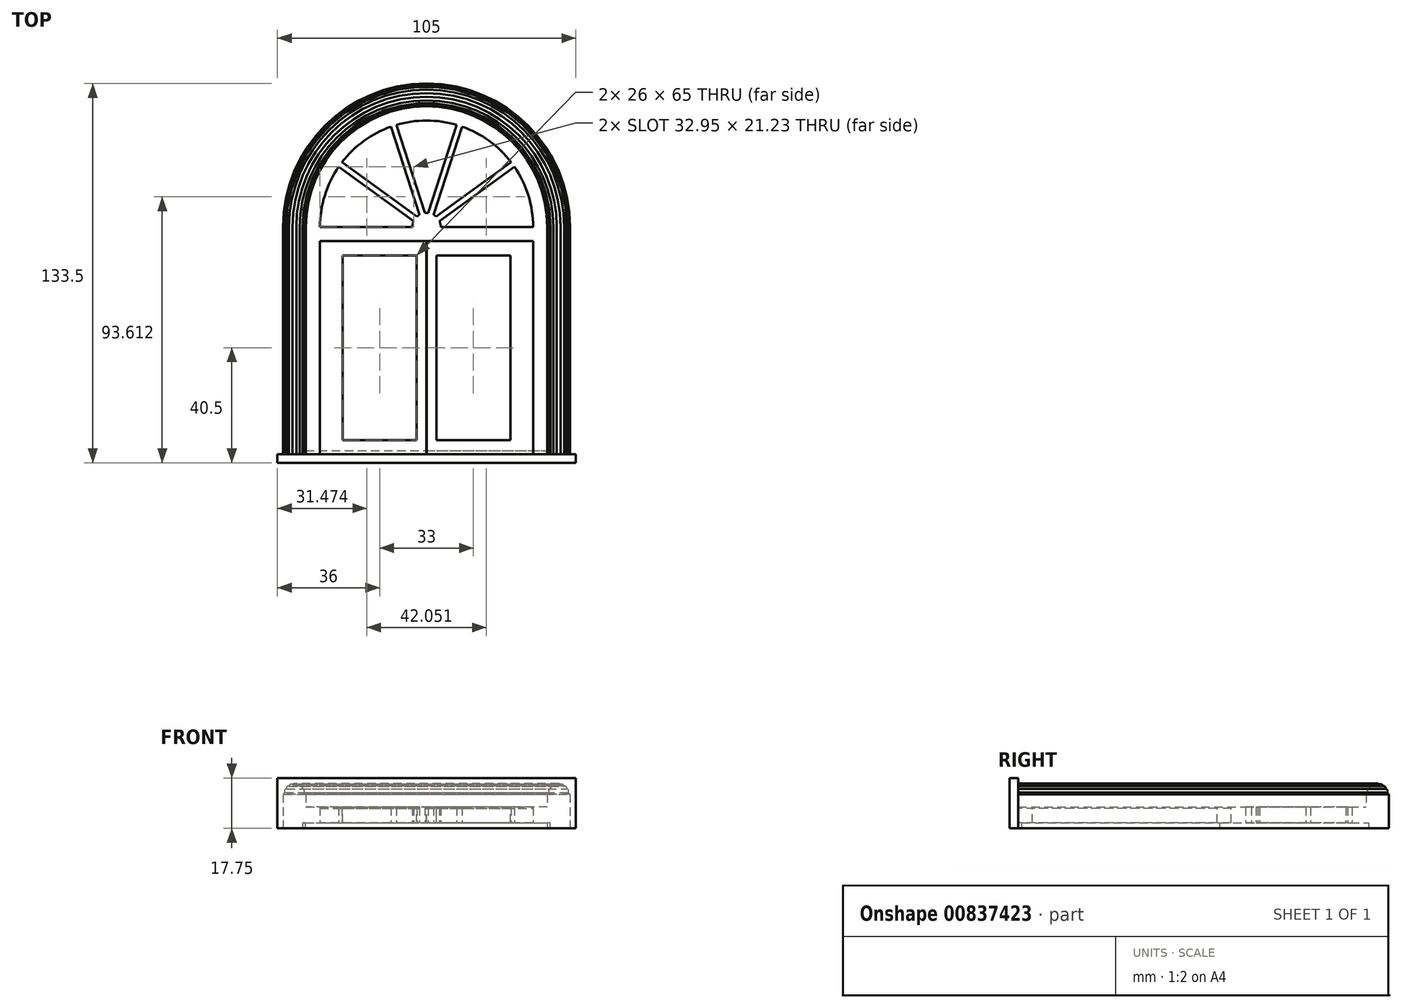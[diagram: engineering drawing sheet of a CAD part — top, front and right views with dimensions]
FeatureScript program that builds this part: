
annotation { "Feature Type Name" : "Feature", "Feature Type Description" : "" }
export const myFeature = defineFeature(function(context is Context, id is Id, definition is map)
    precondition{}
    {
        {
            var Q0;
            Q0=qCreatedBy(makeId("Top.planeOp"),FACE);
            var sketch = newSketch(context, id + "F0", { "sketchPlane" : qUnion([Q0])});
            skLineSegment(sketch, "E0.bottom", {"start": v(-37.5, 75) * mm, "end": v(37.5, 75) * mm});
            skLineSegment(sketch, "E0.top", {"start": v(-37.5, 0) * mm, "end": v(37.5, 0) * mm});
            skLineSegment(sketch, "E0.left", {"start": v(-37.5, 75) * mm, "end": v(-37.5, 0) * mm});
            skLineSegment(sketch, "E0.right", {"start": v(37.5, 75) * mm, "end": v(37.5, 0) * mm});
            skPoint(sketch, "E1", {"position": v(0, 0) * mm});
            skSolve(sketch);
        }
        {
            var Q0;
            Q0=qSketchRegion(id+"F0",true);
            extrude(context, id + "F1", {"entities" : qUnion([Q0]), "depth" : 5 * mm, "offsetDistance" : 25 * mm});
        }
        {
            var Q0;
            Q0=makeQuery(id+"F1.opExtrude","CAP_FACE",FACE,{"disambiguationData":[OSD([sQuery(id+"F0.wireOp",EDGE,"E0.bottom"),sQuery(id+"F0.wireOp",EDGE,"E0.top"),sQuery(id+"F0.wireOp",EDGE,"E0.left"),sQuery(id+"F0.wireOp",EDGE,"E0.right")])],"isStart":false});
            var sketch = newSketch(context, id + "F2", { "sketchPlane" : qUnion([Q0])});
            skLineSegment(sketch, "E2.bottom", {"start": v(3.5, 70) * mm, "end": v(29.5, 70) * mm});
            skLineSegment(sketch, "E2.top", {"start": v(3.5, 5) * mm, "end": v(29.5, 5) * mm});
            skLineSegment(sketch, "E2.left", {"start": v(3.5, 70) * mm, "end": v(3.5, 5) * mm});
            skLineSegment(sketch, "E2.right", {"start": v(29.5, 70) * mm, "end": v(29.5, 5) * mm});
            skLineSegment(sketch, "E3.bottom", {"start": v(-29.5, 70) * mm, "end": v(-3.5, 70) * mm});
            skLineSegment(sketch, "E3.top", {"start": v(-29.5, 5) * mm, "end": v(-3.5, 5) * mm});
            skLineSegment(sketch, "E3.left", {"start": v(-29.5, 70) * mm, "end": v(-29.5, 5) * mm});
            skLineSegment(sketch, "E3.right", {"start": v(-3.5, 70) * mm, "end": v(-3.5, 5) * mm});
            skLineSegment(sketch, "E4.bottom", {"start": v(-0.05, 75) * mm, "end": v(0.05, 75) * mm});
            skLineSegment(sketch, "E4.top", {"start": v(-0.05, 0) * mm, "end": v(0.05, 0) * mm});
            skLineSegment(sketch, "E4.left", {"start": v(-0.05, 75) * mm, "end": v(-0.05, 0) * mm});
            skLineSegment(sketch, "E4.right", {"start": v(0.05, 75) * mm, "end": v(0.05, 0) * mm});
            skSolve(sketch);
        }
        {
            var Q0;
            Q0=qSketchRegion(id+"F2",true);
            extrude(context, id + "F3", {"entities" : qUnion([Q0]), "operationType" : NewBodyOperationType.REMOVE, "oppositeDirection" : true, "depth" : 5 * mm, "offsetDistance" : 25 * mm});
        }
        {
            var Q0;
            Q0=qCreatedBy(makeId("Top.planeOp"),FACE);
            var sketch = newSketch(context, id + "F4", { "sketchPlane" : qUnion([Q0])});
            skLineSegment(sketch, "E5.bottom", {"start": v(-42.5, 0) * mm, "end": v(-37.5, 0) * mm});
            skLineSegment(sketch, "E5.left", {"start": v(-42.5, 0) * mm, "end": v(-42.5, 80) * mm});
            skLineSegment(sketch, "E5.right", {"start": v(-37.5, 0) * mm, "end": v(-37.5, 75) * mm});
            skLineSegment(sketch, "E6", {"start": v(0, 0) * mm, "end": v(0, 80) * mm, "construction": true});
            skLineSegment(sketch, "E7.bottom", {"start": v(-37.5, 80) * mm, "end": v(-5, 80) * mm});
            skLineSegment(sketch, "E7.top", {"start": v(-37.5, 75) * mm, "end": v(0, 75) * mm});
            skLineSegment(sketch, "E7.right", {"start": v(0, 80) * mm, "end": v(0, 75) * mm});
            skArc(sketch, "E8", {"start": v(0, 117.5) * mm, "mid": v(-5.37, 117.11) * mm, "end": v(-10.63, 115.96) * mm});
            skArc(sketch, "E9", {"start": v(0, 122.5) * mm, "mid": v(-30.05, 110.05) * mm, "end": v(-42.5, 80) * mm});
            skLineSegment(sketch, "E10.trimOffspring", {"start": v(0, 117.5) * mm, "end": v(0, 122.5) * mm});
            skArc(sketch, "E11", {"start": v(0, 85) * mm, "mid": v(-0.28, 85) * mm, "end": v(-0.56, 84.97) * mm});
            skLineSegment(sketch, "E12", {"start": v(-34.38, 104.98) * mm, "end": v(0, 80) * mm, "construction": true});
            skLineSegment(sketch, "E13", {"start": v(-13.13, 120.42) * mm, "end": v(0, 80) * mm, "construction": true});
            skLineSegment(sketch, "E14", {"start": v(-30.92, 101.23) * mm, "end": v(-4.55, 82.07) * mm});
            skLineSegment(sketch, "E15", {"start": v(-3.38, 83.69) * mm, "end": v(-29.74, 102.84) * mm});
            skPoint(sketch, "E16", {"position": v(-30.33, 102.03) * mm});
            skPoint(sketch, "E17", {"position": v(-3.96, 82.88) * mm});
            skLineSegment(sketch, "E18", {"start": v(-10.63, 115.96) * mm, "end": v(-0.56, 84.97) * mm});
            skLineSegment(sketch, "E19", {"start": v(-2.46, 84.35) * mm, "end": v(-12.54, 115.34) * mm});
            skPoint(sketch, "E20", {"position": v(-11.58, 115.65) * mm});
            skPoint(sketch, "E21", {"position": v(-1.51, 84.66) * mm});
            skLineSegment(sketch, "E22", {"start": v(0, 80) * mm, "end": v(0, 85) * mm});
            skArc(sketch, "E23.trimOffspring", {"start": v(-30.92, 101.23) * mm, "mid": v(-35.82, 91.11) * mm, "end": v(-37.5, 80) * mm});
            skArc(sketch, "E24.trimOffspring", {"start": v(-12.54, 115.34) * mm, "mid": v(-22.04, 110.34) * mm, "end": v(-29.74, 102.84) * mm});
            skArc(sketch, "E25.trimOffspring", {"start": v(-4.55, 82.07) * mm, "mid": v(-4.89, 81.06) * mm, "end": v(-5, 80) * mm});
            skArc(sketch, "E26.trimOffspring", {"start": v(-2.46, 84.35) * mm, "mid": v(-2.94, 84.05) * mm, "end": v(-3.38, 83.69) * mm});
            skArc(sketch, "E27.MirrorCS", {"start": v(4.55, 82.07) * mm, "mid": v(4.89, 81.06) * mm, "end": v(5, 80) * mm});
            skArc(sketch, "E28.MirrorCS", {"start": v(0, 85) * mm, "mid": v(0.28, 85) * mm, "end": v(0.56, 84.97) * mm});
            skArc(sketch, "E29.MirrorCS", {"start": v(2.46, 84.35) * mm, "mid": v(2.94, 84.05) * mm, "end": v(3.38, 83.69) * mm});
            skLineSegment(sketch, "E30.MirrorCS", {"start": v(42.5, 0) * mm, "end": v(37.5, 0) * mm});
            skLineSegment(sketch, "E31.MirrorCS", {"start": v(37.5, 80) * mm, "end": v(5, 80) * mm});
            skLineSegment(sketch, "E32.MirrorCS", {"start": v(37.5, 75) * mm, "end": v(0, 75) * mm});
            skPoint(sketch, "E33.MirrorP", {"position": v(1.51, 84.66) * mm});
            skArc(sketch, "E34.MirrorCS", {"start": v(30.92, 101.23) * mm, "mid": v(35.82, 91.11) * mm, "end": v(37.5, 80) * mm});
            skLineSegment(sketch, "E35.MirrorCS", {"start": v(2.46, 84.35) * mm, "end": v(12.54, 115.34) * mm});
            skPoint(sketch, "E36.MirrorP", {"position": v(11.58, 115.65) * mm});
            skArc(sketch, "E37.MirrorCS", {"start": v(0, 117.5) * mm, "mid": v(5.37, 117.11) * mm, "end": v(10.63, 115.96) * mm});
            skLineSegment(sketch, "E38.MirrorCS", {"start": v(3.38, 83.69) * mm, "end": v(29.74, 102.84) * mm});
            skLineSegment(sketch, "E39.MirrorCS", {"start": v(13.13, 120.42) * mm, "end": v(0, 80) * mm, "construction": true});
            skArc(sketch, "E40.MirrorCS", {"start": v(0, 122.5) * mm, "mid": v(30.05, 110.05) * mm, "end": v(42.5, 80) * mm});
            skLineSegment(sketch, "E41.MirrorCS", {"start": v(10.63, 115.96) * mm, "end": v(0.56, 84.97) * mm});
            skPoint(sketch, "E42.MirrorP", {"position": v(30.33, 102.03) * mm});
            skLineSegment(sketch, "E43.MirrorCS", {"start": v(42.5, 0) * mm, "end": v(42.5, 80) * mm});
            skLineSegment(sketch, "E44.MirrorCS", {"start": v(34.38, 104.98) * mm, "end": v(0, 80) * mm, "construction": true});
            skArc(sketch, "E45.MirrorCS", {"start": v(12.54, 115.34) * mm, "mid": v(22.04, 110.34) * mm, "end": v(29.74, 102.84) * mm});
            skLineSegment(sketch, "E46.MirrorCS", {"start": v(30.92, 101.23) * mm, "end": v(4.55, 82.07) * mm});
            skLineSegment(sketch, "E47.MirrorCS", {"start": v(37.5, 0) * mm, "end": v(37.5, 75) * mm});
            skPoint(sketch, "E48.MirrorP", {"position": v(3.96, 82.88) * mm});
            skSolve(sketch);
        }
        {
            var Q0;
            Q0=qSketchRegion(id+"F4",true);
            extrude(context, id + "F5", {"entities" : qUnion([Q0]), "operationType" : NewBodyOperationType.ADD, "depth" : 5.5 * mm, "offsetDistance" : 25 * mm});
        }
        {
            var Q0;
            Q0=qCreatedBy(makeId("Top.planeOp"),FACE);
            var sketch = newSketch(context, id + "F6", { "sketchPlane" : qUnion([Q0])});
            skLineSegment(sketch, "E49.bottom", {"start": v(-42.5, 0) * mm, "end": v(-50.5, 0) * mm});
            skLineSegment(sketch, "E49.left", {"start": v(-42.5, 0) * mm, "end": v(-42.5, 80) * mm});
            skLineSegment(sketch, "E49.right", {"start": v(-50.5, 0) * mm, "end": v(-50.5, 80) * mm});
            skArc(sketch, "E50", {"start": v(0, 122.5) * mm, "mid": v(-30.05, 110.05) * mm, "end": v(-42.5, 80) * mm});
            skArc(sketch, "E51", {"start": v(0, 130.5) * mm, "mid": v(-35.7, 115.7) * mm, "end": v(-50.5, 80) * mm});
            skLineSegment(sketch, "E52", {"start": v(0, 122.5) * mm, "end": v(0, 130.5) * mm});
            skLineSegment(sketch, "E53.MirrorCS", {"start": v(42.5, 0) * mm, "end": v(50.5, 0) * mm});
            skLineSegment(sketch, "E54.MirrorCS", {"start": v(42.5, 0) * mm, "end": v(42.5, 80) * mm});
            skLineSegment(sketch, "E55.MirrorCS", {"start": v(50.5, 0) * mm, "end": v(50.5, 80) * mm});
            skArc(sketch, "E56.MirrorCS", {"start": v(0, 122.5) * mm, "mid": v(30.05, 110.05) * mm, "end": v(42.5, 80) * mm});
            skArc(sketch, "E57.MirrorCS", {"start": v(0, 130.5) * mm, "mid": v(35.7, 115.7) * mm, "end": v(50.5, 80) * mm});
            skSolve(sketch);
        }
        {
            var Q0;
            Q0=qSketchRegion(id+"F6",true);
            extrude(context, id + "F7", {"entities" : qUnion([Q0]), "operationType" : NewBodyOperationType.ADD, "depth" : 10 * mm, "offsetDistance" : 25 * mm});
        }
        {
            var Q0;
            Q0=makeQuery(id+"F5.opExtrude","SWEPT_FACE",FACE,{"disambiguationData":[OSD([sQuery(id+"F4.wireOp",EDGE,"E31.MirrorCS")])]});
            var sketch = newSketch(context, id + "F8", { "sketchPlane" : qUnion([Q0])});
            skLineSegment(sketch, "E58", {"start": v(46.5, 10) * mm, "end": v(44, 10) * mm});
            skCircle(sketch, "E59", {"center": v(46.5, 10) * mm, "radius": 3 * mm, "construction": true});
            skArc(sketch, "E60", {"start": v(50.25, 10) * mm, "mid": v(50.14, 10.39) * mm, "end": v(49.85, 10.67) * mm});
            skArc(sketch, "E61.1.0", {"start": v(49.85, 10.67) * mm, "mid": v(49.96, 11.44) * mm, "end": v(49.34, 11.9) * mm});
            skArc(sketch, "E61.2.0", {"start": v(49.34, 11.9) * mm, "mid": v(49.15, 12.65) * mm, "end": v(48.4, 12.84) * mm});
            skArc(sketch, "E61.3.0", {"start": v(48.4, 12.84) * mm, "mid": v(47.94, 13.46) * mm, "end": v(47.17, 13.35) * mm});
            skArc(sketch, "E61.4.0", {"start": v(47.17, 13.35) * mm, "mid": v(46.5, 13.75) * mm, "end": v(45.83, 13.35) * mm});
            skArc(sketch, "E61.5.0", {"start": v(45.83, 13.35) * mm, "mid": v(45.06, 13.46) * mm, "end": v(44.6, 12.84) * mm});
            skArc(sketch, "E61.6.0", {"start": v(44.6, 12.84) * mm, "mid": v(43.85, 12.65) * mm, "end": v(43.66, 11.9) * mm});
            skArc(sketch, "E61.7.0", {"start": v(43.66, 11.9) * mm, "mid": v(43.04, 11.44) * mm, "end": v(43.15, 10.67) * mm});
            skArc(sketch, "E61.8.0", {"start": v(43.15, 10.67) * mm, "mid": v(42.86, 10.39) * mm, "end": v(42.75, 10) * mm});
            skLineSegment(sketch, "E61.anchor2", {"start": v(46.5, 10) * mm, "end": v(44.25, 10) * mm, "construction": true});
            skLineSegment(sketch, "E62", {"start": v(46.5, 10) * mm, "end": v(50.25, 10) * mm});
            skLineSegment(sketch, "E63", {"start": v(50.25, 10) * mm, "end": v(42.75, 10) * mm});
            skLineSegment(sketch, "E64.MirrorCS", {"start": v(-46.5, 10) * mm, "end": v(-44, 10) * mm});
            skArc(sketch, "E65.MirrorCS", {"start": v(-49.85, 10.67) * mm, "mid": v(-49.96, 11.44) * mm, "end": v(-49.34, 11.9) * mm});
            skArc(sketch, "E66.MirrorCS", {"start": v(-45.83, 13.35) * mm, "mid": v(-45.06, 13.46) * mm, "end": v(-44.6, 12.84) * mm});
            skArc(sketch, "E67.MirrorCS", {"start": v(-50.25, 10) * mm, "mid": v(-50.14, 10.39) * mm, "end": v(-49.85, 10.67) * mm});
            skArc(sketch, "E68.MirrorCS", {"start": v(-44.6, 12.84) * mm, "mid": v(-43.85, 12.65) * mm, "end": v(-43.66, 11.9) * mm});
            skArc(sketch, "E69.MirrorCS", {"start": v(-47.17, 13.35) * mm, "mid": v(-46.5, 13.75) * mm, "end": v(-45.83, 13.35) * mm});
            skLineSegment(sketch, "E70.MirrorCS", {"start": v(-46.5, 10) * mm, "end": v(-44.25, 10) * mm, "construction": true});
            skArc(sketch, "E71.MirrorCS", {"start": v(-43.15, 10.67) * mm, "mid": v(-42.86, 10.39) * mm, "end": v(-42.75, 10) * mm});
            skArc(sketch, "E72.MirrorCS", {"start": v(-49.34, 11.9) * mm, "mid": v(-49.15, 12.65) * mm, "end": v(-48.4, 12.84) * mm});
            skArc(sketch, "E73.MirrorCS", {"start": v(-43.66, 11.9) * mm, "mid": v(-43.04, 11.44) * mm, "end": v(-43.15, 10.67) * mm});
            skArc(sketch, "E74.MirrorCS", {"start": v(-48.4, 12.84) * mm, "mid": v(-47.94, 13.46) * mm, "end": v(-47.17, 13.35) * mm});
            skLineSegment(sketch, "E75.MirrorCS", {"start": v(-46.5, 10) * mm, "end": v(-50.25, 10) * mm});
            skLineSegment(sketch, "E76.MirrorCS", {"start": v(-50.25, 10) * mm, "end": v(-42.75, 10) * mm});
            skCircle(sketch, "E77.MirrorC", {"center": v(-46.5, 10) * mm, "radius": 3 * mm, "construction": true});
            skSolve(sketch);
        }
        {
            var Q0;
            Q0=qSketchRegion(id+"F8",true);
            var Q1;
            Q1=makeQuery(id+"F7.opExtrude","CAP_EDGE",EDGE,{"disambiguationData":[OSD([sQuery(id+"F6.wireOp",EDGE,"E50"),sQuery(id+"F6.wireOp",EDGE,"E56.MirrorCS")])],"isStart":false});
            sweep(context, id + "F9", {"operationType" : NewBodyOperationType.ADD, "profiles" : qUnion([Q0]), "path" : qUnion([Q1])});
        }
        {
            var Q0;
            Q0=makeQuery(id+"F7.opExtrude","CAP_FACE",FACE,{"disambiguationData":[OSD([sQuery(id+"F6.wireOp",EDGE,"E49.bottom"),sQuery(id+"F6.wireOp",EDGE,"E49.left"),sQuery(id+"F6.wireOp",EDGE,"E49.right"),sQuery(id+"F6.wireOp",EDGE,"E50"),sQuery(id+"F6.wireOp",EDGE,"E51"),sQuery(id+"F6.wireOp",EDGE,"E53.MirrorCS"),sQuery(id+"F6.wireOp",EDGE,"E54.MirrorCS"),sQuery(id+"F6.wireOp",EDGE,"E55.MirrorCS"),sQuery(id+"F6.wireOp",EDGE,"E56.MirrorCS"),sQuery(id+"F6.wireOp",EDGE,"E57.MirrorCS")])],"isStart":false});
            var sketch = newSketch(context, id + "F10", { "sketchPlane" : qUnion([Q0])});
            skLineSegment(sketch, "E78", {"start": v(0, 80) * mm, "end": v(0, 130.5) * mm, "construction": true});
            skLineSegment(sketch, "E79", {"start": v(0, 80) * mm, "end": v(6.15, 130.12) * mm, "construction": true});
            skLineSegment(sketch, "E80", {"start": v(0, 80) * mm, "end": v(-6.15, 130.12) * mm, "construction": true});
            skLineSegment(sketch, "E81", {"start": v(-6.15, 130.12) * mm, "end": v(-5.18, 122.18) * mm});
            skLineSegment(sketch, "E82", {"start": v(6.15, 130.12) * mm, "end": v(5.18, 122.18) * mm});
            skArc(sketch, "E83", {"start": v(6.15, 130.12) * mm, "mid": v(0, 130.5) * mm, "end": v(-6.15, 130.12) * mm});
            skArc(sketch, "E84", {"start": v(5.18, 122.18) * mm, "mid": v(0, 122.5) * mm, "end": v(-5.18, 122.18) * mm});
            skSolve(sketch);
        }
        {
            var Q0;
            Q0=qSketchRegion(id+"F8",true);
            var Q1;
            Q1=makeQuery(id+"F7.opExtrude","CAP_EDGE",EDGE,{"disambiguationData":[OSD([sQuery(id+"F6.wireOp",EDGE,"E49.left")])],"isStart":false});
            sweep(context, id + "F11", {"operationType" : NewBodyOperationType.ADD, "profiles" : qUnion([Q0]), "path" : qUnion([Q1])});
        }
        {
            var Q0;
            {var subQ0=sQuery(id+"F6.wireOp",EDGE,"E49.left");var subQ1=sQuery(id+"F6.wireOp",EDGE,"E49.bottom");Q0=makeQuery(id+"F11.boolean.opBoolean","MERGE",FACE,{"derivedFrom":[makeQuery(id+"F7.boolean.opBoolean","MERGE",FACE,{"derivedFrom":[makeQuery(id+"F5.boolean.opBoolean","MERGE",FACE,{"derivedFrom":[makeQuery(id+"F1.opExtrude","SWEPT_FACE",FACE,{"disambiguationData":[OSD([sQuery(id+"F0.wireOp",EDGE,"E0.top")])]}),makeQuery(id+"F5.opExtrude","SWEPT_FACE",FACE,{"disambiguationData":[OSD([sQuery(id+"F4.wireOp",EDGE,"E5.bottom")])]}),makeQuery(id+"F5.opExtrude","SWEPT_FACE",FACE,{"disambiguationData":[OSD([sQuery(id+"F4.wireOp",EDGE,"E30.MirrorCS")])]})]}),makeQuery(id+"F7.opExtrude","SWEPT_FACE",FACE,{"disambiguationData":[OSD([subQ1])]}),makeQuery(id+"F7.opExtrude","SWEPT_FACE",FACE,{"disambiguationData":[OSD([sQuery(id+"F6.wireOp",EDGE,"E53.MirrorCS")])]})]}),makeQuery(id+"F11.opSweep","CAP_FACE",FACE,{"disambiguationData":[OSD([subQ1,subQ0,sQuery(id+"F8.wireOp",EDGE,"E60"),sQuery(id+"F8.wireOp",EDGE,"E61.1.0"),sQuery(id+"F8.wireOp",EDGE,"E61.2.0"),sQuery(id+"F8.wireOp",EDGE,"E61.3.0"),sQuery(id+"F8.wireOp",EDGE,"E61.4.0"),sQuery(id+"F8.wireOp",EDGE,"E61.5.0"),sQuery(id+"F8.wireOp",EDGE,"E61.6.0"),sQuery(id+"F8.wireOp",EDGE,"E61.7.0"),sQuery(id+"F8.wireOp",EDGE,"E61.8.0"),sQuery(id+"F8.wireOp",EDGE,"E63")])],"isStart":false}),makeQuery(id+"F11.opSweep","CAP_FACE",FACE,{"disambiguationData":[OSD([subQ1,subQ0,sQuery(id+"F8.wireOp",EDGE,"E65.MirrorCS"),sQuery(id+"F8.wireOp",EDGE,"E66.MirrorCS"),sQuery(id+"F8.wireOp",EDGE,"E67.MirrorCS"),sQuery(id+"F8.wireOp",EDGE,"E68.MirrorCS"),sQuery(id+"F8.wireOp",EDGE,"E69.MirrorCS"),sQuery(id+"F8.wireOp",EDGE,"E71.MirrorCS"),sQuery(id+"F8.wireOp",EDGE,"E72.MirrorCS"),sQuery(id+"F8.wireOp",EDGE,"E73.MirrorCS"),sQuery(id+"F8.wireOp",EDGE,"E74.MirrorCS"),sQuery(id+"F8.wireOp",EDGE,"E76.MirrorCS")])],"isStart":false})]});}
            var sketch = newSketch(context, id + "F12", { "sketchPlane" : qUnion([Q0])});
            skLineSegment(sketch, "E85.bottom", {"start": v(-52.5, 0) * mm, "end": v(52.5, 0) * mm});
            skLineSegment(sketch, "E85.top", {"start": v(-52.5, 15.75) * mm, "end": v(52.5, 15.75) * mm});
            skLineSegment(sketch, "E85.left", {"start": v(-52.5, 0) * mm, "end": v(-52.5, 15.75) * mm});
            skLineSegment(sketch, "E85.right", {"start": v(52.5, 0) * mm, "end": v(52.5, 15.75) * mm});
            skSolve(sketch);
        }
        {
            var Q0;
            Q0=qSketchRegion(id+"F12",true);
            extrude(context, id + "F13", {"entities" : qUnion([Q0]), "operationType" : NewBodyOperationType.ADD, "depth" : 3 * mm, "offsetDistance" : 25 * mm});
        }
        {
            var Q0;
            Q0=makeQuery(id+"F13.boolean.opBoolean","MERGE",FACE,{"derivedFrom":[makeQuery(id+"F7.boolean.opBoolean","MERGE",FACE,{"derivedFrom":[makeQuery(id+"F5.boolean.opBoolean","MERGE",FACE,{"derivedFrom":[makeQuery(id+"F1.opExtrude","CAP_FACE",FACE,{"disambiguationData":[OSD([sQuery(id+"F0.wireOp",EDGE,"E0.bottom"),sQuery(id+"F0.wireOp",EDGE,"E0.top"),sQuery(id+"F0.wireOp",EDGE,"E0.left"),sQuery(id+"F0.wireOp",EDGE,"E0.right")])],"isStart":true}),makeQuery(id+"F5.opExtrude","CAP_FACE",FACE,{"disambiguationData":[OSD([sQuery(id+"F4.wireOp",EDGE,"E5.bottom"),sQuery(id+"F4.wireOp",EDGE,"E5.left"),sQuery(id+"F4.wireOp",EDGE,"E5.right"),sQuery(id+"F4.wireOp",EDGE,"E7.top"),sQuery(id+"F4.wireOp",EDGE,"E8"),sQuery(id+"F4.wireOp",EDGE,"E9"),sQuery(id+"F4.wireOp",EDGE,"E7.bottom"),sQuery(id+"F4.wireOp",EDGE,"E11"),sQuery(id+"F4.wireOp",EDGE,"E14"),sQuery(id+"F4.wireOp",EDGE,"E15"),sQuery(id+"F4.wireOp",EDGE,"E18"),sQuery(id+"F4.wireOp",EDGE,"E19"),sQuery(id+"F4.wireOp",EDGE,"E23.trimOffspring"),sQuery(id+"F4.wireOp",EDGE,"E24.trimOffspring"),sQuery(id+"F4.wireOp",EDGE,"E25.trimOffspring"),sQuery(id+"F4.wireOp",EDGE,"E26.trimOffspring"),sQuery(id+"F4.wireOp",EDGE,"E27.MirrorCS"),sQuery(id+"F4.wireOp",EDGE,"E28.MirrorCS"),sQuery(id+"F4.wireOp",EDGE,"E29.MirrorCS"),sQuery(id+"F4.wireOp",EDGE,"E30.MirrorCS"),sQuery(id+"F4.wireOp",EDGE,"E32.MirrorCS"),sQuery(id+"F4.wireOp",EDGE,"E34.MirrorCS"),sQuery(id+"F4.wireOp",EDGE,"E35.MirrorCS"),sQuery(id+"F4.wireOp",EDGE,"E37.MirrorCS"),sQuery(id+"F4.wireOp",EDGE,"E38.MirrorCS"),sQuery(id+"F4.wireOp",EDGE,"E31.MirrorCS"),sQuery(id+"F4.wireOp",EDGE,"E40.MirrorCS"),sQuery(id+"F4.wireOp",EDGE,"E41.MirrorCS"),sQuery(id+"F4.wireOp",EDGE,"E43.MirrorCS"),sQuery(id+"F4.wireOp",EDGE,"E45.MirrorCS"),sQuery(id+"F4.wireOp",EDGE,"E46.MirrorCS"),sQuery(id+"F4.wireOp",EDGE,"E47.MirrorCS")])],"isStart":true})]}),makeQuery(id+"F7.opExtrude","CAP_FACE",FACE,{"disambiguationData":[OSD([sQuery(id+"F6.wireOp",EDGE,"E49.bottom"),sQuery(id+"F6.wireOp",EDGE,"E49.left"),sQuery(id+"F6.wireOp",EDGE,"E49.right"),sQuery(id+"F6.wireOp",EDGE,"E50"),sQuery(id+"F6.wireOp",EDGE,"E51"),sQuery(id+"F6.wireOp",EDGE,"E53.MirrorCS"),sQuery(id+"F6.wireOp",EDGE,"E54.MirrorCS"),sQuery(id+"F6.wireOp",EDGE,"E55.MirrorCS"),sQuery(id+"F6.wireOp",EDGE,"E56.MirrorCS"),sQuery(id+"F6.wireOp",EDGE,"E57.MirrorCS")])],"isStart":true})]}),makeQuery(id+"F13.opExtrude","SWEPT_FACE",FACE,{"disambiguationData":[OSD([sQuery(id+"F12.wireOp",EDGE,"E85.bottom")])]})]});
            var sketch = newSketch(context, id + "F14", { "sketchPlane" : qUnion([Q0])});
            skLineSegment(sketch, "E86.bottom", {"start": v(-50.5, 3) * mm, "end": v(-42.56, 3) * mm});
            skLineSegment(sketch, "E86.left", {"start": v(-50.5, 3) * mm, "end": v(-50.5, -80) * mm});
            skLineSegment(sketch, "E86.right", {"start": v(50.5, 3) * mm, "end": v(50.5, -80) * mm});
            skArc(sketch, "E87", {"start": v(-50.5, -80) * mm, "mid": v(0, -130.5) * mm, "end": v(50.5, -80) * mm});
            skLineSegment(sketch, "E88.left", {"start": v(-42.56, -1.25) * mm, "end": v(-42.56, -71) * mm});
            skLineSegment(sketch, "E88.right", {"start": v(42.56, -1.25) * mm, "end": v(42.56, -71) * mm});
            skArc(sketch, "E89", {"start": v(-42.56, -71) * mm, "mid": v(0, -123.5) * mm, "end": v(42.56, -71) * mm});
            skLineSegment(sketch, "E90.trimOffspring", {"start": v(42.56, 3) * mm, "end": v(50.5, 3) * mm});
            skLineSegment(sketch, "E91.left", {"start": v(-42.56, 3) * mm, "end": v(-42.56, 3) * mm});
            skLineSegment(sketch, "E91.right", {"start": v(42.56, 3) * mm, "end": v(42.56, 3) * mm});
            skLineSegment(sketch, "E92.bottom", {"start": v(-42.56, 3) * mm, "end": v(42.56, 3) * mm});
            skLineSegment(sketch, "E92.top", {"start": v(-42.56, -1.25) * mm, "end": v(42.56, -1.25) * mm});
            skLineSegment(sketch, "E93.bottom", {"start": v(-50.5, 3) * mm, "end": v(-52.5, 3) * mm});
            skLineSegment(sketch, "E93.top", {"start": v(-50.5, 0) * mm, "end": v(-52.5, 0) * mm});
            skLineSegment(sketch, "E93.left", {"start": v(-50.5, 3) * mm, "end": v(-50.5, 0) * mm});
            skLineSegment(sketch, "E93.right", {"start": v(-52.5, 3) * mm, "end": v(-52.5, 0) * mm});
            skLineSegment(sketch, "E94.bottom", {"start": v(50.5, 3) * mm, "end": v(52.5, 3) * mm});
            skLineSegment(sketch, "E94.top", {"start": v(50.5, 0) * mm, "end": v(52.5, 0) * mm});
            skLineSegment(sketch, "E94.left", {"start": v(50.5, 3) * mm, "end": v(50.5, 0) * mm});
            skLineSegment(sketch, "E94.right", {"start": v(52.5, 3) * mm, "end": v(52.5, 0) * mm});
            skSolve(sketch);
        }
        {
            var Q0;
            {var subQ3=sQuery(id+"F2.wireOp",EDGE,"E4.left");var subQ7=sQuery(id+"F14.wireOp",EDGE,"E92.top");var subQ12=makeQuery(id+"F3.boolean.opBoolean","COPY",EDGE,{"derivedFrom":makeQuery(id+"F3.opExtrude","CAP_EDGE",EDGE,{"disambiguationData":[OSD([subQ3])],"isStart":false})});var subQ13=makeQuery(id+"F14.imprint","INTERSECT",VERTEX,{"derivedFrom":[subQ12,subQ7]});var subQ18=sQuery(id+"F14.wireOp",EDGE,"E94.bottom");var subQ20=sQuery(id+"F14.wireOp",EDGE,"E86.bottom");var subQ24=sQuery(id+"F14.wireOp",EDGE,"E93.bottom");Q0=qUnion([makeQuery(id+"F14.imprint","IMPRINT",FACE,{"disambiguationData":[TD([[makeQuery(id+"F14.imprint","IMPRINT",EDGE,{"derivedFrom":subQ24}),-1.0]])]}),makeQuery(id+"F14.imprint","IMPRINT",FACE,{"disambiguationData":[TD([[makeQuery(id+"F14.imprint","IMPRINT",EDGE,{"derivedFrom":subQ18}),-1.0]])]}),makeQuery(id+"F14.imprint","IMPRINT",FACE,{"disambiguationData":[TD([[makeQuery(id+"F14.imprint","IMPRINT",EDGE,{"disambiguationData":[TD([[subQ13,-1.0]])],"derivedFrom":subQ7}),1.0]])]}),makeQuery(id+"F14.imprint","IMPRINT",FACE,{"disambiguationData":[TD([[makeQuery(id+"F14.imprint","IMPRINT",EDGE,{"derivedFrom":subQ20}),-1.0]])]})]);}
            extrude(context, id + "F15", {"entities" : qUnion([Q0]), "operationType" : NewBodyOperationType.ADD, "depth" : 2 * mm, "offsetDistance" : 25 * mm});
        }
    });
